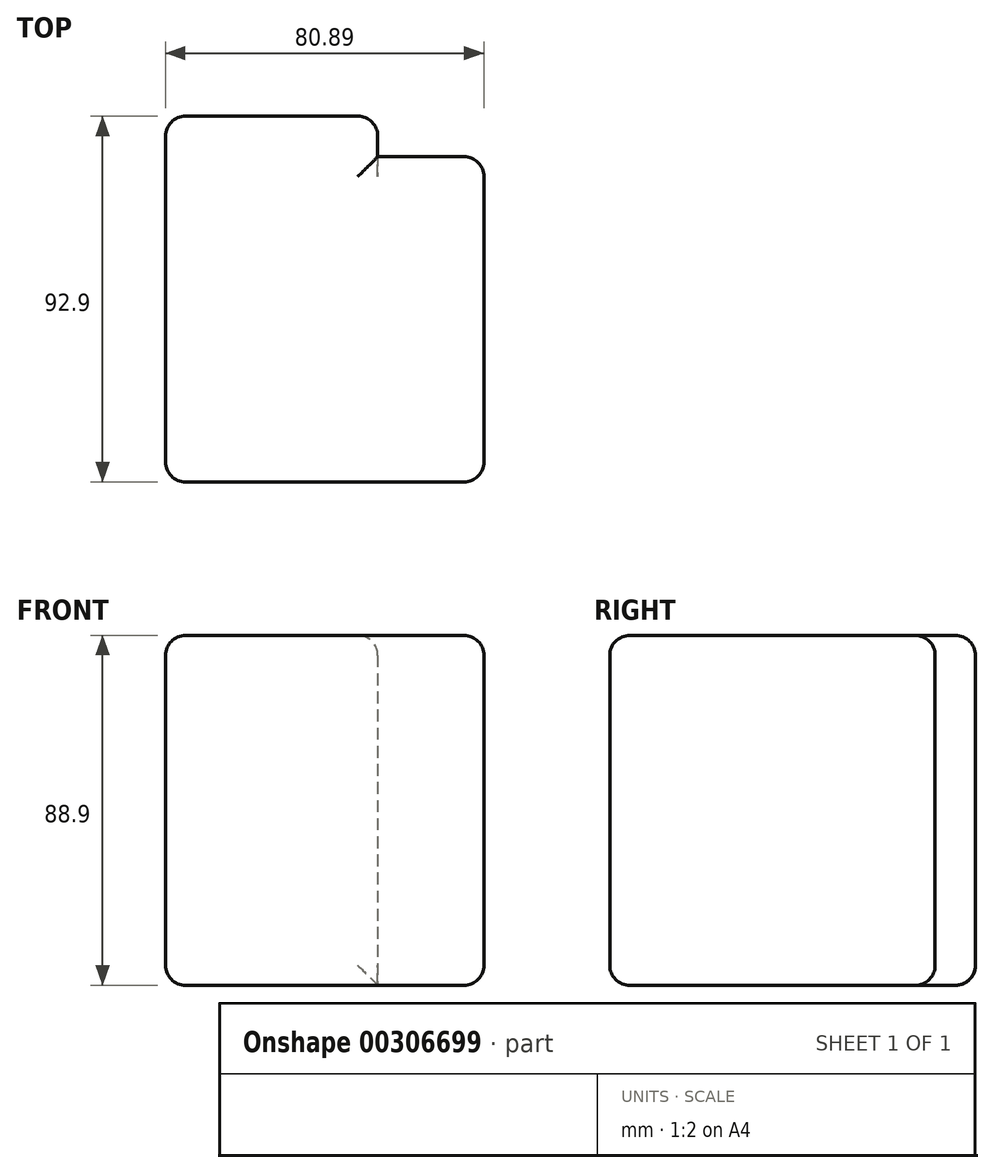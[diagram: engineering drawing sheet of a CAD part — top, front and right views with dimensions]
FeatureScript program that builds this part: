
annotation { "Feature Type Name" : "Feature", "Feature Type Description" : "" }
export const myFeature = defineFeature(function(context is Context, id is Id, definition is map)
    precondition{}
    {
        {
            var Q0;
            Q0=qCreatedBy(makeId("Top.planeOp"),FACE);
            var sketch = newSketch(context, id + "F0", { "sketchPlane" : qUnion([Q0])});
            skLineSegment(sketch, "E0.bottom", {"start": v(-43.38, 42.2) * mm, "end": v(10.55, 42.2) * mm});
            skLineSegment(sketch, "E0.top", {"start": v(-43.38, 31.95) * mm, "end": v(10.55, 31.95) * mm});
            skLineSegment(sketch, "E0.left", {"start": v(-43.38, 42.2) * mm, "end": v(-43.38, 31.95) * mm});
            skLineSegment(sketch, "E0.right", {"start": v(10.55, 42.2) * mm, "end": v(10.55, 31.95) * mm});
            skLineSegment(sketch, "E1.bottom", {"start": v(-43.38, 31.95) * mm, "end": v(37.51, 31.95) * mm});
            skLineSegment(sketch, "E1.top", {"start": v(-43.38, -50.7) * mm, "end": v(37.51, -50.7) * mm});
            skLineSegment(sketch, "E1.left", {"start": v(-43.38, 31.95) * mm, "end": v(-43.38, -50.7) * mm});
            skLineSegment(sketch, "E1.right", {"start": v(37.51, 31.95) * mm, "end": v(37.51, -50.7) * mm});
            skSolve(sketch);
        }
        {
            var Q0;
            Q0 = qSketchRegion(id + "F0", true);
            extrude(context, id + "F1", {"entities" : qUnion([Q0]), "depth" : 88.9 * mm});
        }
        {
            var Q0;
            Q0=makeQuery(id+"F1.opExtrude","CAP_EDGE",EDGE,{"disambiguationData":[OSD([sQuery(id+"F0.wireOp",EDGE,"E1.bottom")])],"isStart":true});
            var Q1;
            Q1=makeQuery(id+"F1.opExtrude","CAP_EDGE",EDGE,{"disambiguationData":[OSD([sQuery(id+"F0.wireOp",EDGE,"E0.bottom")])],"isStart":true});
            var Q2;
            Q2=makeQuery(id+"F1.opExtrude","SWEPT_EDGE",EDGE,{"disambiguationData":[OSD([sQuery(id+"F0.wireOp",EDGE,"E0.bottom"),sQuery(id+"F0.wireOp",EDGE,"E0.right")])]});
            var Q3;
            Q3=makeQuery(id+"F1.opExtrude","SWEPT_EDGE",EDGE,{"disambiguationData":[OSD([sQuery(id+"F0.wireOp",EDGE,"E0.bottom"),sQuery(id+"F0.wireOp",EDGE,"E0.left")])]});
            var Q4;
            Q4=makeQuery(id+"F1.opExtrude","CAP_EDGE",EDGE,{"disambiguationData":[OSD([sQuery(id+"F0.wireOp",EDGE,"E0.left"),sQuery(id+"F0.wireOp",EDGE,"E1.left")])],"isStart":true});
            var Q5;
            Q5=makeQuery(id+"F1.opExtrude","CAP_EDGE",EDGE,{"disambiguationData":[OSD([sQuery(id+"F0.wireOp",EDGE,"E1.top")])],"isStart":true});
            var Q6;
            Q6=makeQuery(id+"F1.opExtrude","CAP_EDGE",EDGE,{"disambiguationData":[OSD([sQuery(id+"F0.wireOp",EDGE,"E1.right")])],"isStart":true});
            var Q7;
            Q7=makeQuery(id+"F1.opExtrude","CAP_EDGE",EDGE,{"disambiguationData":[OSD([sQuery(id+"F0.wireOp",EDGE,"E0.left"),sQuery(id+"F0.wireOp",EDGE,"E1.left")])],"isStart":false});
            var Q8;
            Q8=makeQuery(id+"F1.opExtrude","SWEPT_FACE",FACE,{"disambiguationData":[OSD([sQuery(id+"F0.wireOp",EDGE,"E1.top")])]});
            var Q9;
            Q9=makeQuery(id+"F1.opExtrude","CAP_EDGE",EDGE,{"disambiguationData":[OSD([sQuery(id+"F0.wireOp",EDGE,"E1.right")])],"isStart":false});
            var Q10;
            Q10=makeQuery(id+"F1.opExtrude","CAP_EDGE",EDGE,{"disambiguationData":[OSD([sQuery(id+"F0.wireOp",EDGE,"E1.bottom")])],"isStart":false});
            var Q11;
            Q11=makeQuery(id+"F1.opExtrude","CAP_FACE",FACE,{"disambiguationData":[OSD([sQuery(id+"F0.wireOp",EDGE,"E0.bottom"),sQuery(id+"F0.wireOp",EDGE,"E0.left"),sQuery(id+"F0.wireOp",EDGE,"E0.right"),sQuery(id+"F0.wireOp",EDGE,"E1.bottom"),sQuery(id+"F0.wireOp",EDGE,"E1.top"),sQuery(id+"F0.wireOp",EDGE,"E1.left"),sQuery(id+"F0.wireOp",EDGE,"E1.right")])],"isStart":false});
            var Q12;
            Q12=makeQuery(id+"F1.opExtrude","SWEPT_EDGE",EDGE,{"disambiguationData":[OSD([sQuery(id+"F0.wireOp",EDGE,"E1.bottom"),sQuery(id+"F0.wireOp",EDGE,"E1.right")])]});
            fillet(context, id + "F2", {"entities" : qUnion([Q0, Q1, Q2, Q3, Q4, Q5, Q6, Q7, Q8, Q9, Q10, Q11, Q12]), "radius" : 5.08 * mm, "tangentPropagation" : true, "allowEdgeOverflow" : false});
        }
    });
